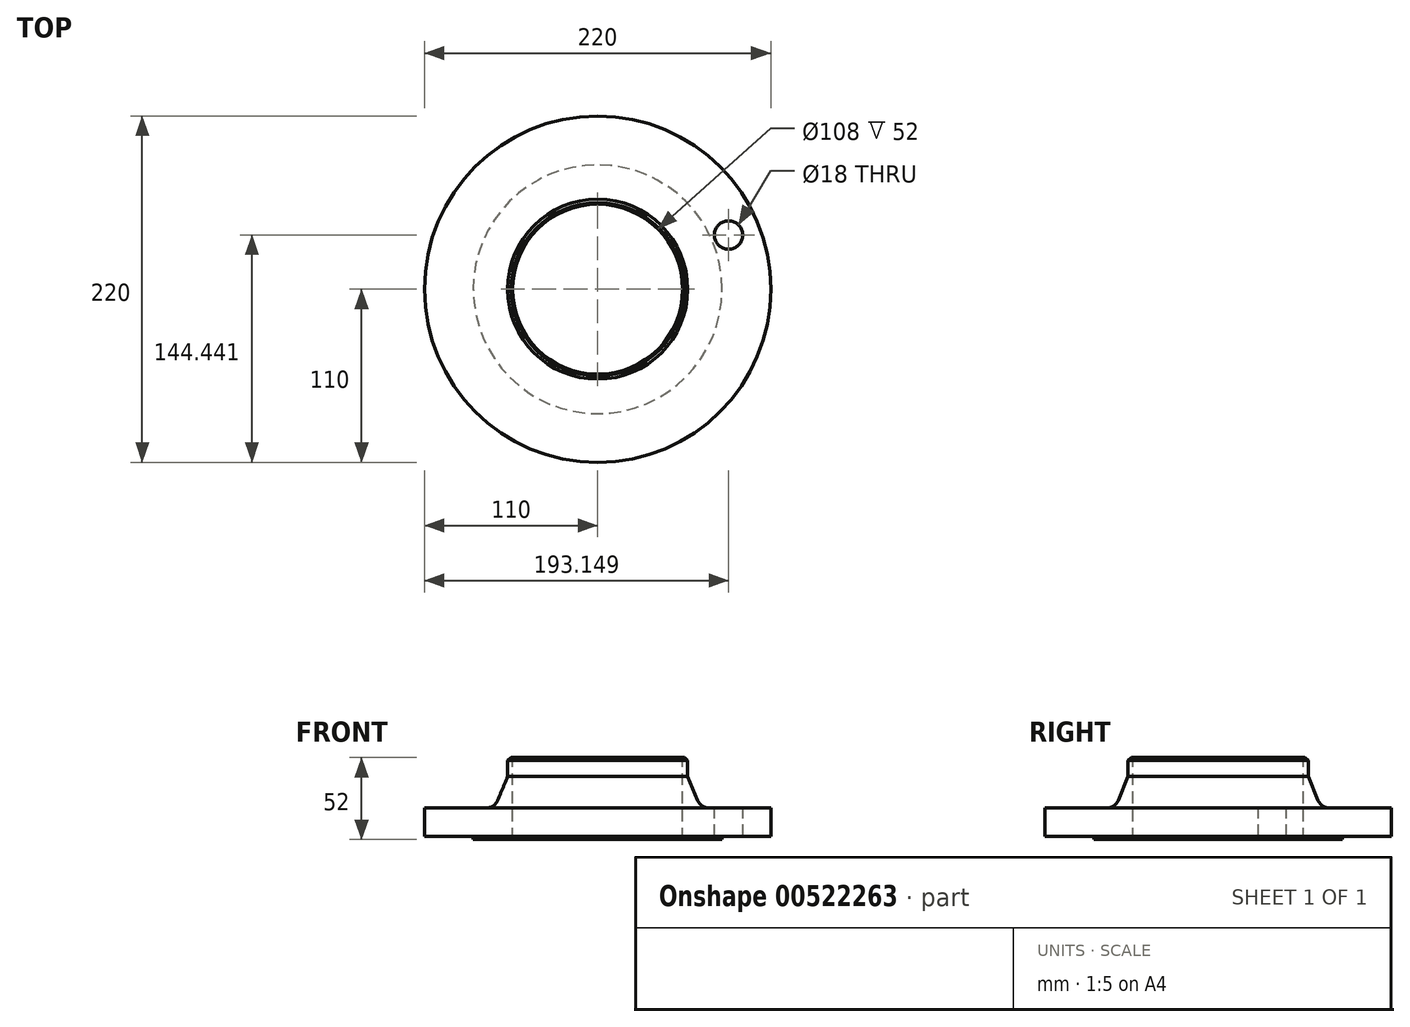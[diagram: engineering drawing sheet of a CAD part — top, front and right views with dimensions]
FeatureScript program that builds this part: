
annotation { "Feature Type Name" : "Feature", "Feature Type Description" : "" }
export const myFeature = defineFeature(function(context is Context, id is Id, definition is map)
    precondition{}
    {
        {
            var Q0;
            Q0=qCreatedBy(makeId("Front.planeOp"),FACE);
            var sketch = newSketch(context, id + "F0", { "sketchPlane" : qUnion([Q0])});
            skLineSegment(sketch, "E0", {"start": v(0, 52) * mm, "end": v(0, 0) * mm});
            skLineSegment(sketch, "E1", {"start": v(54, 0) * mm, "end": v(79, 0) * mm});
            skLineSegment(sketch, "E2", {"start": v(79, 0) * mm, "end": v(79, 2) * mm});
            skLineSegment(sketch, "E3", {"start": v(79, 2) * mm, "end": v(110, 2) * mm});
            skLineSegment(sketch, "E4", {"start": v(110, 2) * mm, "end": v(110, 20) * mm});
            skLineSegment(sketch, "E5", {"start": v(110, 20) * mm, "end": v(65.5, 20) * mm});
            skLineSegment(sketch, "E6", {"start": v(65.5, 20) * mm, "end": v(57.15, 40) * mm});
            skLineSegment(sketch, "E7", {"start": v(57.15, 40) * mm, "end": v(57.15, 52) * mm});
            skLineSegment(sketch, "E8", {"start": v(57.15, 52) * mm, "end": v(54, 52) * mm});
            skLineSegment(sketch, "E9", {"start": v(54, 52) * mm, "end": v(54, 0) * mm});
            skSolve(sketch);
        }
        {
            var Q0;
            Q0=makeQuery(id+"F0.imprint","IMPRINT",FACE,{"disambiguationData":[TD([[makeQuery(id+"F0.imprint","IMPRINT",EDGE,{"derivedFrom":sQuery(id+"F0.wireOp",EDGE,"E1")}),1.0]])]});
            var Q1;
            Q1=sQuery(id+"F0.wireOp",EDGE,"E0");
            revolve(context, id + "F1", {"entities" : qUnion([Q0]), "axis" : qUnion([Q1]), "revolveType" : RevolveType.FULL});
        }
        {
            var Q0;
            Q0=makeQuery(id+"F1.opRevolve","SWEPT_FACE",FACE,{"disambiguationData":[OSD([sQuery(id+"F0.wireOp",EDGE,"E5")])]});
            var sketch = newSketch(context, id + "F2", { "sketchPlane" : qUnion([Q0])});
            skCircle(sketch, "E10", {"center": v(83.15, 34.44) * mm, "radius": 9 * mm});
            skLineSegment(sketch, "E11", {"start": v(83.15, 34.44) * mm, "end": v(0, 0) * mm});
            skSolve(sketch);
        }
        {
            var Q0;
            Q0=makeQuery(id+"F2.imprint","IMPRINT",FACE,{"disambiguationData":[TD([[makeQuery(id+"F2.imprint","IMPRINT",EDGE,{"derivedFrom":sQuery(id+"F2.wireOp",EDGE,"E10")}),1.0]])]});
            extrude(context, id + "F3", {"entities" : qUnion([Q0]), "operationType" : NewBodyOperationType.REMOVE, "endBound" : BoundingType.THROUGH_ALL, "oppositeDirection" : true, "depth" : 25 * mm});
        }
        {
            var Q0;
            Q0=qCreatedBy(makeId("Front.planeOp"),FACE);
            var sketch = newSketch(context, id + "F4", { "sketchPlane" : qUnion([Q0])});
            skLineSegment(sketch, "E12", {"start": v(55, 52) * mm, "end": v(55, 52) * mm});
            skLineSegment(sketch, "E13", {"start": v(55, 52) * mm, "end": v(57.15, 50.35) * mm});
            skLineSegment(sketch, "E14", {"start": v(57.15, 50.35) * mm, "end": v(57.15, 52) * mm});
            skLineSegment(sketch, "E15", {"start": v(57.15, 52) * mm, "end": v(55, 52) * mm});
            skSolve(sketch);
        }
        {
            var Q0;
            Q0=qSketchRegion(id+"F4",true);
            var Q1;
            Q1=sQuery(id+"F0.wireOp",EDGE,"E0");
            revolve(context, id + "F5", {"operationType" : NewBodyOperationType.REMOVE, "entities" : qUnion([Q0]), "axis" : qUnion([Q1]), "revolveType" : RevolveType.FULL, "oppositeDirection" : true});
        }
        {
            var Q0;
            Q0=makeQuery(id+"F1.opRevolve","SWEPT_EDGE",EDGE,{"disambiguationData":[OSD([sQuery(id+"F0.wireOp",EDGE,"E5"),sQuery(id+"F0.wireOp",EDGE,"E6")])]});
            fillet(context, id + "F6", {"entities" : qUnion([Q0]), "radius" : 8 * mm, "tangentPropagation" : true, "allowEdgeOverflow" : false});
        }
    });
